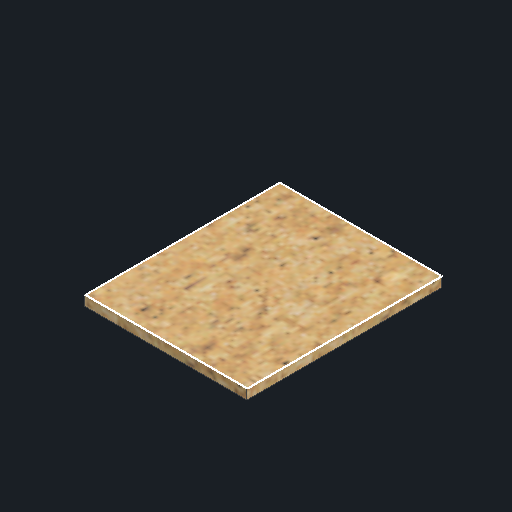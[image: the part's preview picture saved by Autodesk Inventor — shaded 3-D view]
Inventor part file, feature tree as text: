
AUTODESK INVENTOR PART (.ipt)
format: ipt  version: 2022 (Build 260153070, 153G)  size: 178,176 bytes
history: native  units: mm
features: other x1, sketch x1, extrude x1
ambient origin geometry x8: Origin, YZ Plane, XZ Plane, XY Plane, X Axis, Y Axis, Z Axis, Center Point
bodies: Body1 (feature_tree)
feature tree (3):
  other  "Твердое тело1"
  sketch  "Эскиз1"
  extrude  "Выдавливание1"  Depth=250.0mm
